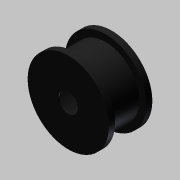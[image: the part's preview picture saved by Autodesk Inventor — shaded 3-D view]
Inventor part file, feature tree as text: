
AUTODESK INVENTOR PART (.ipt)
format: ipt  version: 2012 SP1 (Build 160190100, 190)  size: 107,008 bytes
history: native  units: in
note: dims shown in document units (in); Inventor stores cm internally (conversion verified against a paired STEP export)
features: extrude x4, sketch x4
ambient origin geometry x8: Origin, YZ Plane, XZ Plane, XY Plane, X Axis, Y Axis, Z Axis, Center Point
bodies: Solid1 (feature_tree)
feature tree (8):
  extrude  "Extrusion1"  Depth=0.1969in
  extrude  "Extrusion2"  Depth=0.8268in
  extrude  "Extrusion3"  Depth=0.8268in
  extrude  "Extrusion4"  Depth=0.6299in
  sketch  "Sketch1"  dims[d0=0.689in d1=0.1969in]
  sketch  "Sketch2"  dims[d2=0.315in d3=0.0in d4=0.8268in]
  sketch  "Sketch3"  dims[d5=0.063in d6=0.0in d7=0.8268in]
  sketch  "Sketch5"  dims[d8=0.063in d9=0.0in d11=0.6299in d12=0.4331in d13=0.0in]
